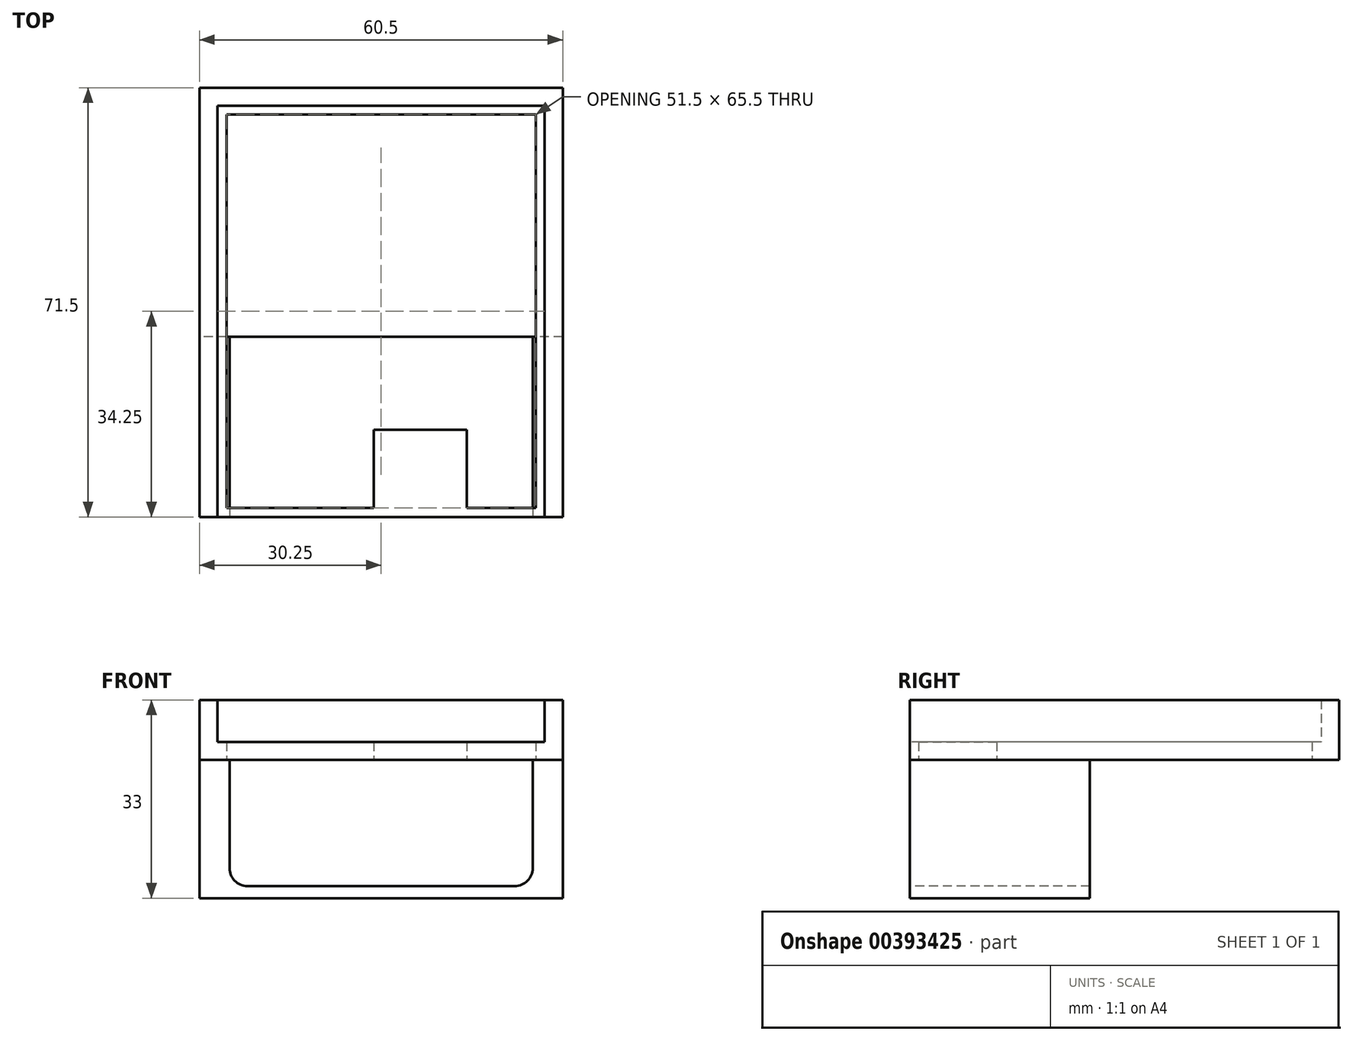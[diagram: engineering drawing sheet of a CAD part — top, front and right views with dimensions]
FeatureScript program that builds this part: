
annotation { "Feature Type Name" : "Feature", "Feature Type Description" : "" }
export const myFeature = defineFeature(function(context is Context, id is Id, definition is map)
    precondition{}
    {
        {
            var Q0;
            Q0=qCreatedBy(makeId("Top.planeOp"),FACE);
            var sketch = newSketch(context, id + "F0", { "sketchPlane" : qUnion([Q0])});
            skLineSegment(sketch, "E0.top", {"start": v(30.25, 35.75) * mm, "end": v(-30.25, 35.75) * mm});
            skLineSegment(sketch, "E0.left", {"start": v(30.25, -35.75) * mm, "end": v(30.25, 35.75) * mm});
            skLineSegment(sketch, "E0.right", {"start": v(-30.25, -35.75) * mm, "end": v(-30.25, 35.75) * mm});
            skPoint(sketch, "E0.middle", {"position": v(0, 0) * mm});
            skLineSegment(sketch, "E1", {"start": v(-30.25, -35.75) * mm, "end": v(-27.25, -35.75) * mm});
            skLineSegment(sketch, "E2", {"start": v(-27.25, -35.75) * mm, "end": v(-27.25, 32.75) * mm});
            skLineSegment(sketch, "E3", {"start": v(-27.25, 32.75) * mm, "end": v(27.25, 32.75) * mm});
            skLineSegment(sketch, "E4", {"start": v(27.25, 32.75) * mm, "end": v(27.25, -35.75) * mm});
            skLineSegment(sketch, "E5", {"start": v(27.25, -35.75) * mm, "end": v(30.25, -35.75) * mm});
            skSolve(sketch);
        }
        {
            var Q0;
            Q0 = qSketchRegion(id + "F0", true);
            extrude(context, id + "F1", {"entities" : qUnion([Q0]), "depth" : 10 * mm});
        }
        {
            var Q0;
            Q0=qCreatedBy(makeId("Top.planeOp"),FACE);
            var sketch = newSketch(context, id + "F2", { "sketchPlane" : qUnion([Q0])});
            skLineSegment(sketch, "E6", {"start": v(-25.75, -35.75) * mm, "end": v(-25.75, 31.25) * mm});
            skLineSegment(sketch, "E7", {"start": v(-25.75, 31.25) * mm, "end": v(25.75, 31.25) * mm});
            skLineSegment(sketch, "E8", {"start": v(25.75, 31.25) * mm, "end": v(25.75, -35.75) * mm});
            skLineSegment(sketch, "E9", {"start": v(25.75, -35.75) * mm, "end": v(27.25, -35.75) * mm});
            skLineSegment(sketch, "E10", {"start": v(27.25, -35.75) * mm, "end": v(27.25, 32.75) * mm});
            skLineSegment(sketch, "E11", {"start": v(27.25, 32.75) * mm, "end": v(-27.25, 32.75) * mm});
            skLineSegment(sketch, "E12", {"start": v(-27.25, 32.75) * mm, "end": v(-27.25, -35.75) * mm});
            skLineSegment(sketch, "E13", {"start": v(-27.25, -35.75) * mm, "end": v(-25.75, -35.75) * mm});
            skLineSegment(sketch, "E14.bottom", {"start": v(-25.75, -35.75) * mm, "end": v(25.75, -35.75) * mm});
            skLineSegment(sketch, "E14.top", {"start": v(-25.75, -34.25) * mm, "end": v(25.75, -34.25) * mm});
            skLineSegment(sketch, "E14.left", {"start": v(-25.75, -35.75) * mm, "end": v(-25.75, -34.25) * mm});
            skLineSegment(sketch, "E14.right", {"start": v(25.75, -35.75) * mm, "end": v(25.75, -34.25) * mm});
            skSolve(sketch);
        }
        {
            var Q0;
            Q0 = qSketchRegion(id + "F2", true);
            extrude(context, id + "F3", {"entities" : qUnion([Q0]), "operationType" : NewBodyOperationType.ADD, "depth" : 3 * mm});
        }
        {
            var Q0;
            Q0=qCreatedBy(makeId("Top.planeOp"),FACE);
            var sketch = newSketch(context, id + "F4", { "sketchPlane" : qUnion([Q0])});
            skLineSegment(sketch, "E15.bottom", {"start": v(30.25, -5.75) * mm, "end": v(-30.25, -5.75) * mm});
            skLineSegment(sketch, "E15.top", {"start": v(30.25, -35.75) * mm, "end": v(-30.25, -35.75) * mm});
            skLineSegment(sketch, "E15.left", {"start": v(30.25, -5.75) * mm, "end": v(30.25, -35.75) * mm});
            skLineSegment(sketch, "E15.right", {"start": v(-30.25, -5.75) * mm, "end": v(-30.25, -35.75) * mm});
            skPoint(sketch, "E15.middle", {"position": v(0, -20.75) * mm});
            skSolve(sketch);
        }
        {
            var Q0;
            Q0 = qSketchRegion(id + "F4", true);
            extrude(context, id + "F5", {"entities" : qUnion([Q0]), "oppositeDirection" : true, "depth" : 23 * mm});
        }
        {
            var Q0;
            Q0=makeQuery(id+"F3.boolean.opBoolean","MERGE",FACE,{"derivedFrom":[makeQuery(id+"F1.opExtrude","CAP_FACE",FACE,{"disambiguationData":[OSD([sQuery(id+"F0.wireOp",EDGE,"E0.top"),sQuery(id+"F0.wireOp",EDGE,"E0.left"),sQuery(id+"F0.wireOp",EDGE,"E0.right"),sQuery(id+"F0.wireOp",EDGE,"E1"),sQuery(id+"F0.wireOp",EDGE,"E2"),sQuery(id+"F0.wireOp",EDGE,"E3"),sQuery(id+"F0.wireOp",EDGE,"E4"),sQuery(id+"F0.wireOp",EDGE,"E5")])],"isStart":true}),makeQuery(id+"F3.opExtrude","CAP_FACE",FACE,{"disambiguationData":[OSD([sQuery(id+"F2.wireOp",EDGE,"E6"),sQuery(id+"F2.wireOp",EDGE,"E7"),sQuery(id+"F2.wireOp",EDGE,"E8"),sQuery(id+"F2.wireOp",EDGE,"E9"),sQuery(id+"F2.wireOp",EDGE,"E10"),sQuery(id+"F2.wireOp",EDGE,"E11"),sQuery(id+"F2.wireOp",EDGE,"E12"),sQuery(id+"F2.wireOp",EDGE,"E13"),sQuery(id+"F2.wireOp",EDGE,"E14.bottom"),sQuery(id+"F2.wireOp",EDGE,"E14.top")])],"isStart":true})]});
            var sketch = newSketch(context, id + "F6", { "sketchPlane" : qUnion([Q0])});
            skLineSegment(sketch, "E16.bottom", {"start": v(-1.25, 34.25) * mm, "end": v(14.25, 34.25) * mm});
            skLineSegment(sketch, "E16.top", {"start": v(-1.25, 21.25) * mm, "end": v(14.25, 21.25) * mm});
            skLineSegment(sketch, "E16.left", {"start": v(-1.25, 34.25) * mm, "end": v(-1.25, 21.25) * mm});
            skLineSegment(sketch, "E16.right", {"start": v(14.25, 34.25) * mm, "end": v(14.25, 21.25) * mm});
            skSolve(sketch);
        }
        {
            var Q0;
            Q0=makeQuery(id+"F5.opExtrude","SWEPT_FACE",FACE,{"disambiguationData":[OSD([sQuery(id+"F4.wireOp",EDGE,"E15.top")])]});
            var sketch = newSketch(context, id + "F7", { "sketchPlane" : qUnion([Q0])});
            skLineSegment(sketch, "E17.bottom", {"start": v(-25.25, 0) * mm, "end": v(25.25, 0) * mm});
            skLineSegment(sketch, "E17.top", {"start": v(-25.25, -21) * mm, "end": v(25.25, -21) * mm});
            skLineSegment(sketch, "E17.left", {"start": v(-25.25, 0) * mm, "end": v(-25.25, -21) * mm});
            skLineSegment(sketch, "E17.right", {"start": v(25.25, 0) * mm, "end": v(25.25, -21) * mm});
            skSolve(sketch);
        }
        {
            var Q0;
            Q0 = qSketchRegion(id + "F7", true);
            extrude(context, id + "F8", {"entities" : qUnion([Q0]), "operationType" : NewBodyOperationType.REMOVE, "oppositeDirection" : true, "depth" : 38.4 * mm});
        }
        {
            var Q0;
            Q0=makeQuery(id+"F8.boolean.opBoolean","COPY",EDGE,{"derivedFrom":makeQuery(id+"F8.opExtrude","SWEPT_EDGE",EDGE,{"disambiguationData":[OSD([sQuery(id+"F7.wireOp",EDGE,"E17.top"),sQuery(id+"F7.wireOp",EDGE,"E17.left")])]})});
            var Q1;
            Q1=makeQuery(id+"F8.boolean.opBoolean","COPY",EDGE,{"derivedFrom":makeQuery(id+"F8.opExtrude","SWEPT_EDGE",EDGE,{"disambiguationData":[OSD([sQuery(id+"F7.wireOp",EDGE,"E17.top"),sQuery(id+"F7.wireOp",EDGE,"E17.right")])]})});
            fillet(context, id + "F9", {"entities" : qUnion([Q0, Q1]), "radius" : 3 * mm, "tangentPropagation" : true, "allowEdgeOverflow" : false});
        }
        {
            var Q0;
            Q0 = qSketchRegion(id + "F6", true);
            extrude(context, id + "F10", {"entities" : qUnion([Q0]), "operationType" : NewBodyOperationType.ADD, "oppositeDirection" : true, "depth" : 3 * mm});
        }
    });
